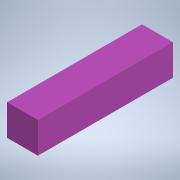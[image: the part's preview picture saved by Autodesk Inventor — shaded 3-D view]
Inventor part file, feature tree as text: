
AUTODESK INVENTOR PART (.ipt)
format: ipt  version: 2022.3 (Build 263350000, 350)  size: 99,840 bytes
history: native  units: in
note: dims shown in document units (in); Inventor stores cm internally (conversion verified against a paired STEP export)
features: extrude x1, sketch x1
ambient origin geometry x8: Origin, YZ Plane, XZ Plane, XY Plane, X Axis, Y Axis, Z Axis, Center Point
bodies: Solid1 (feature_tree)
feature tree (2):
  extrude  "Extrusion1"  Depth=2.0in
  sketch  "Sketch1"  dims[d0=8.75in d1=2.0in d2=2.0in d3=0.0in]
